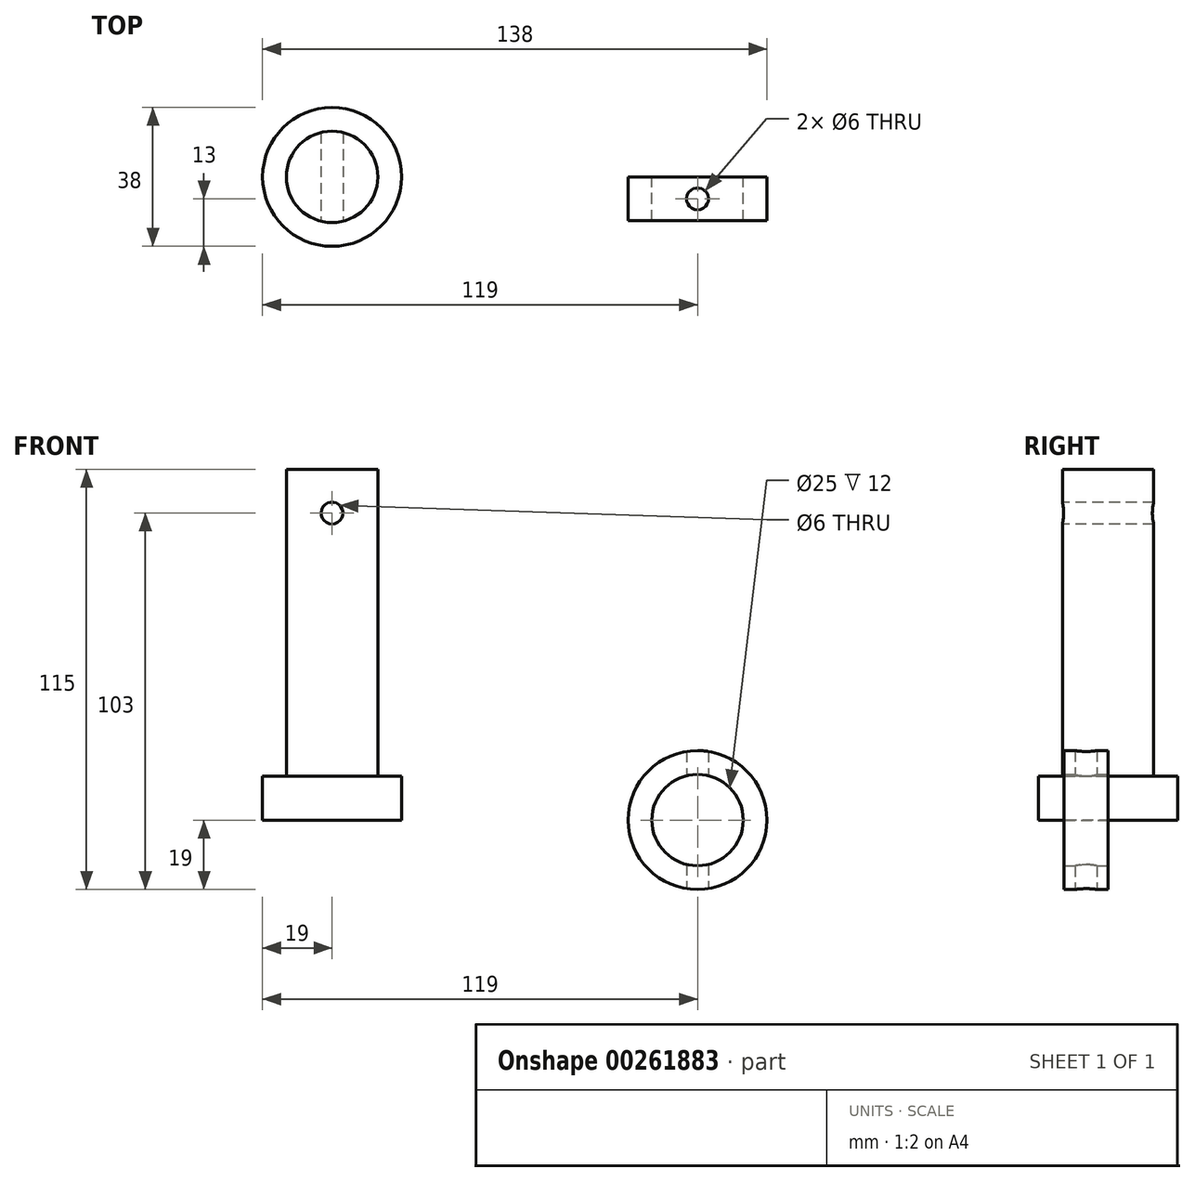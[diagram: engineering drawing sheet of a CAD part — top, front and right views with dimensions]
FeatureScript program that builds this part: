
annotation { "Feature Type Name" : "Feature", "Feature Type Description" : "" }
export const myFeature = defineFeature(function(context is Context, id is Id, definition is map)
    precondition{}
    {
        {
            var Q0;
            Q0=qCreatedBy(makeId("Top.planeOp"),FACE);
            var sketch = newSketch(context, id + "F0", { "sketchPlane" : qUnion([Q0])});
            skCircle(sketch, "E0", {"center": v(0, 0) * mm, "radius": 19 * mm});
            skCircle(sketch, "E1", {"center": v(0, 0) * mm, "radius": 12.5 * mm});
            skSolve(sketch);
        }
        {
            var Q0;
            Q0=makeQuery(id+"F0.imprint","IMPRINT",FACE,{"disambiguationData":[TD([[makeQuery(id+"F0.imprint","IMPRINT",EDGE,{"derivedFrom":sQuery(id+"F0.wireOp",EDGE,"E1")}),1.0]])]});
            extrude(context, id + "F1", {"entities" : qUnion([Q0]), "depth" : 96 * mm});
        }
        {
            var Q0;
            Q0=makeQuery(id+"F0.imprint","IMPRINT",FACE,{"disambiguationData":[TD([[makeQuery(id+"F0.imprint","IMPRINT",EDGE,{"derivedFrom":sQuery(id+"F0.wireOp",EDGE,"E0")}),1.0]])]});
            extrude(context, id + "F2", {"entities" : qUnion([Q0]), "operationType" : NewBodyOperationType.ADD, "depth" : 12 * mm});
        }
        {
            var Q0;
            Q0=qCreatedBy(makeId("Front.planeOp"),FACE);
            var sketch = newSketch(context, id + "F3", { "sketchPlane" : qUnion([Q0])});
            skCircle(sketch, "E2", {"center": v(100, 0) * mm, "radius": 19 * mm});
            skCircle(sketch, "E3", {"center": v(100, 0) * mm, "radius": 12.5 * mm});
            skSolve(sketch);
        }
        {
            var Q0;
            Q0=makeQuery(id+"F3.imprint","IMPRINT",FACE,{"disambiguationData":[TD([[makeQuery(id+"F3.imprint","IMPRINT",EDGE,{"derivedFrom":sQuery(id+"F3.wireOp",EDGE,"E2")}),1.0]])]});
            extrude(context, id + "F4", {"entities" : qUnion([Q0]), "depth" : 12 * mm});
        }
        {
            var Q0;
            Q0=qCreatedBy(makeId("Front.planeOp"),FACE);
            var sketch = newSketch(context, id + "F5", { "sketchPlane" : qUnion([Q0])});
            skCircle(sketch, "E4", {"center": v(0, 84) * mm, "radius": 3 * mm});
            skSolve(sketch);
        }
        {
            var Q0;
            Q0 = qSketchRegion(id + "F5", true);
            extrude(context, id + "F6", {"entities" : qUnion([Q0]), "operationType" : NewBodyOperationType.REMOVE, "endBound" : BoundingType.SYMMETRIC, "oppositeDirection" : true, "depth" : 25 * mm});
        }
        {
            var Q0;
            Q0=qCreatedBy(makeId("Top.planeOp"),FACE);
            var sketch = newSketch(context, id + "F7", { "sketchPlane" : qUnion([Q0])});
            skCircle(sketch, "E5", {"center": v(100, -6) * mm, "radius": 3 * mm});
            skLineSegment(sketch, "E6.0", {"start": v(119, 0) * mm, "end": v(81, 0) * mm});
            skLineSegment(sketch, "E7.0", {"start": v(119, -12) * mm, "end": v(81, -12) * mm});
            skSolve(sketch);
        }
        {
            var Q0;
            Q0 = qSketchRegion(id + "F7", true);
            extrude(context, id + "F8", {"entities" : qUnion([Q0]), "operationType" : NewBodyOperationType.REMOVE, "endBound" : BoundingType.SYMMETRIC, "depth" : 72.4 * mm});
        }
    });
